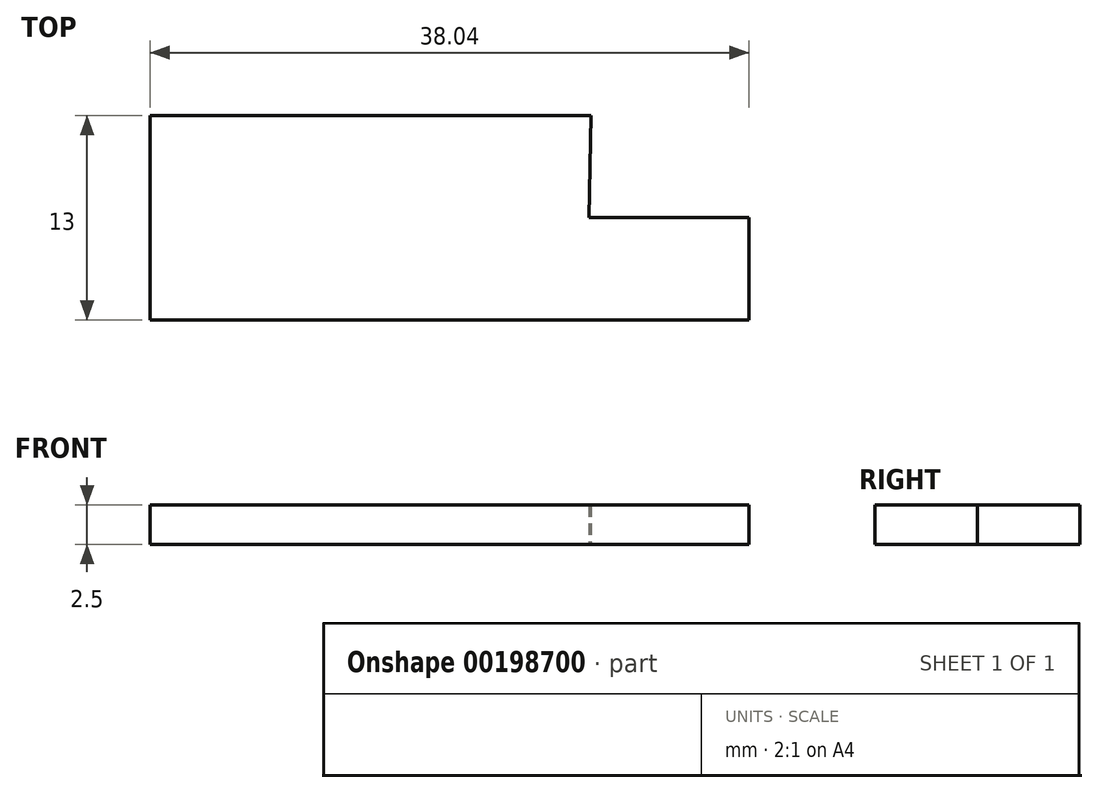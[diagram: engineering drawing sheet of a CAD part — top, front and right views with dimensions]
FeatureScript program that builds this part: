
annotation { "Feature Type Name" : "Feature", "Feature Type Description" : "" }
export const myFeature = defineFeature(function(context is Context, id is Id, definition is map)
    precondition{}
    {
        {
            var Q0;
            Q0=qCreatedBy(makeId("Top.planeOp"),FACE);
            var sketch = newSketch(context, id + "F0", { "sketchPlane" : qUnion([Q0])});
            skLineSegment(sketch, "E0", {"start": v(-20.07, -4.77) * mm, "end": v(-20.07, 8.23) * mm});
            skLineSegment(sketch, "E1", {"start": v(-20.07, 8.23) * mm, "end": v(7.93, 8.23) * mm});
            skLineSegment(sketch, "E2", {"start": v(-20.07, -4.77) * mm, "end": v(17.97, -4.77) * mm});
            skLineSegment(sketch, "E3", {"start": v(17.97, -4.77) * mm, "end": v(17.97, 1.73) * mm});
            skLineSegment(sketch, "E4", {"start": v(17.97, 1.73) * mm, "end": v(7.8, 1.73) * mm});
            skLineSegment(sketch, "E5", {"start": v(7.8, 1.73) * mm, "end": v(7.93, 8.23) * mm});
            skSolve(sketch);
        }
        {
            var Q0;
            Q0=makeQuery(id+"F0.imprint","IMPRINT",FACE,{"disambiguationData":[TD([[makeQuery(id+"F0.imprint","IMPRINT",EDGE,{"derivedFrom":sQuery(id+"F0.wireOp",EDGE,"E0")}),-1.0]])]});
            extrude(context, id + "F1", {"entities" : qUnion([Q0]), "depth" : 2.5 * mm});
        }
    });
